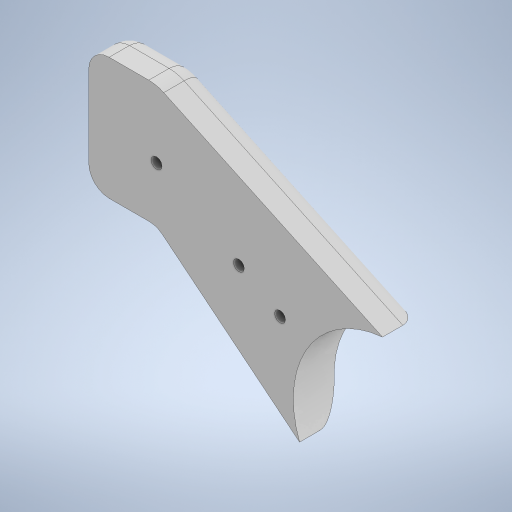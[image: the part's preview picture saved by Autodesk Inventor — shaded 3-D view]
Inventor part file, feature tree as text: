
AUTODESK INVENTOR PART (.ipt)
format: ipt  version: 2024.2 (Build 282272000, 272)  size: 357,376 bytes
history: native  units: mm
features: fillet x3, other x1, extrude x1, mirror x1, sketch x1
ambient origin geometry x8: Origin, YZ Plane, XZ Plane, XY Plane, X Axis, Y Axis, Z Axis, Center Point
bodies: Body1 (feature_tree)
feature tree (7):
  other  "Bryła2"
  extrude  "Wyciągnięcie proste3"  Depth=25.0mm
  fillet  "Zaokrąglenie4"  Radius=29.0mm
  fillet  "Zaokrąglenie6"  Radius=8.0mm
  fillet  "Zaokrąglenie8"  Radius=40.0mm
  mirror  "Odbij1"
  sketch  "Szkic1"
